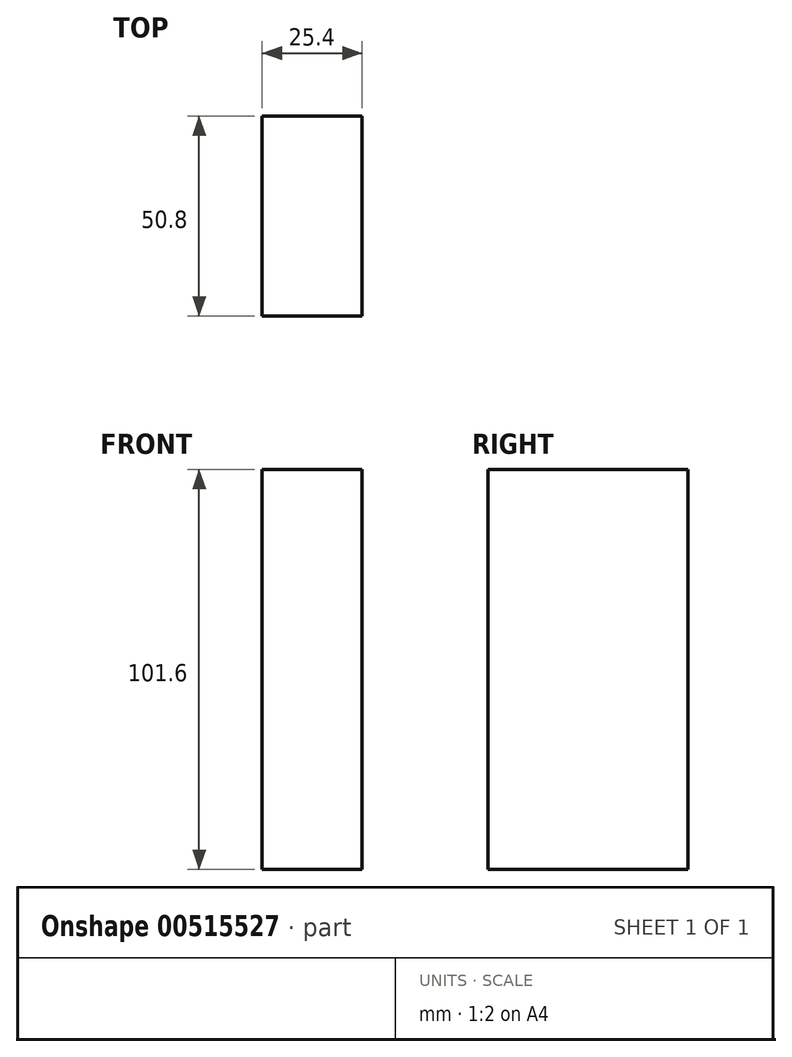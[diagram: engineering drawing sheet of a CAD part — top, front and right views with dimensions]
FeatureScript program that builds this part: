
annotation { "Feature Type Name" : "Feature", "Feature Type Description" : "" }
export const myFeature = defineFeature(function(context is Context, id is Id, definition is map)
    precondition{}
    {
        {
            var Q0;
            Q0=qCreatedBy(makeId("Right.planeOp"),FACE);
            var sketch = newSketch(context, id + "F0", { "sketchPlane" : qUnion([Q0])});
            skLineSegment(sketch, "E0", {"start": v(-25.4, -50.8) * mm, "end": v(-25.4, 50.8) * mm});
            skLineSegment(sketch, "E1", {"start": v(-25.4, 50.8) * mm, "end": v(25.4, 50.8) * mm});
            skLineSegment(sketch, "E2", {"start": v(25.4, 50.8) * mm, "end": v(25.4, -50.8) * mm});
            skLineSegment(sketch, "E3", {"start": v(25.4, -50.8) * mm, "end": v(-25.4, -50.8) * mm});
            skSolve(sketch);
        }
        {
            var Q0;
            Q0=makeQuery(id+"F0.imprint","IMPRINT",FACE,{"disambiguationData":[TD([[makeQuery(id+"F0.imprint","IMPRINT",EDGE,{"derivedFrom":sQuery(id+"F0.wireOp",EDGE,"E0")}),-1.0]])]});
            extrude(context, id + "F1", {"entities" : qUnion([Q0]), "depth" : 25.4 * mm, "offsetDistance" : 25.4 * mm});
        }
    });
